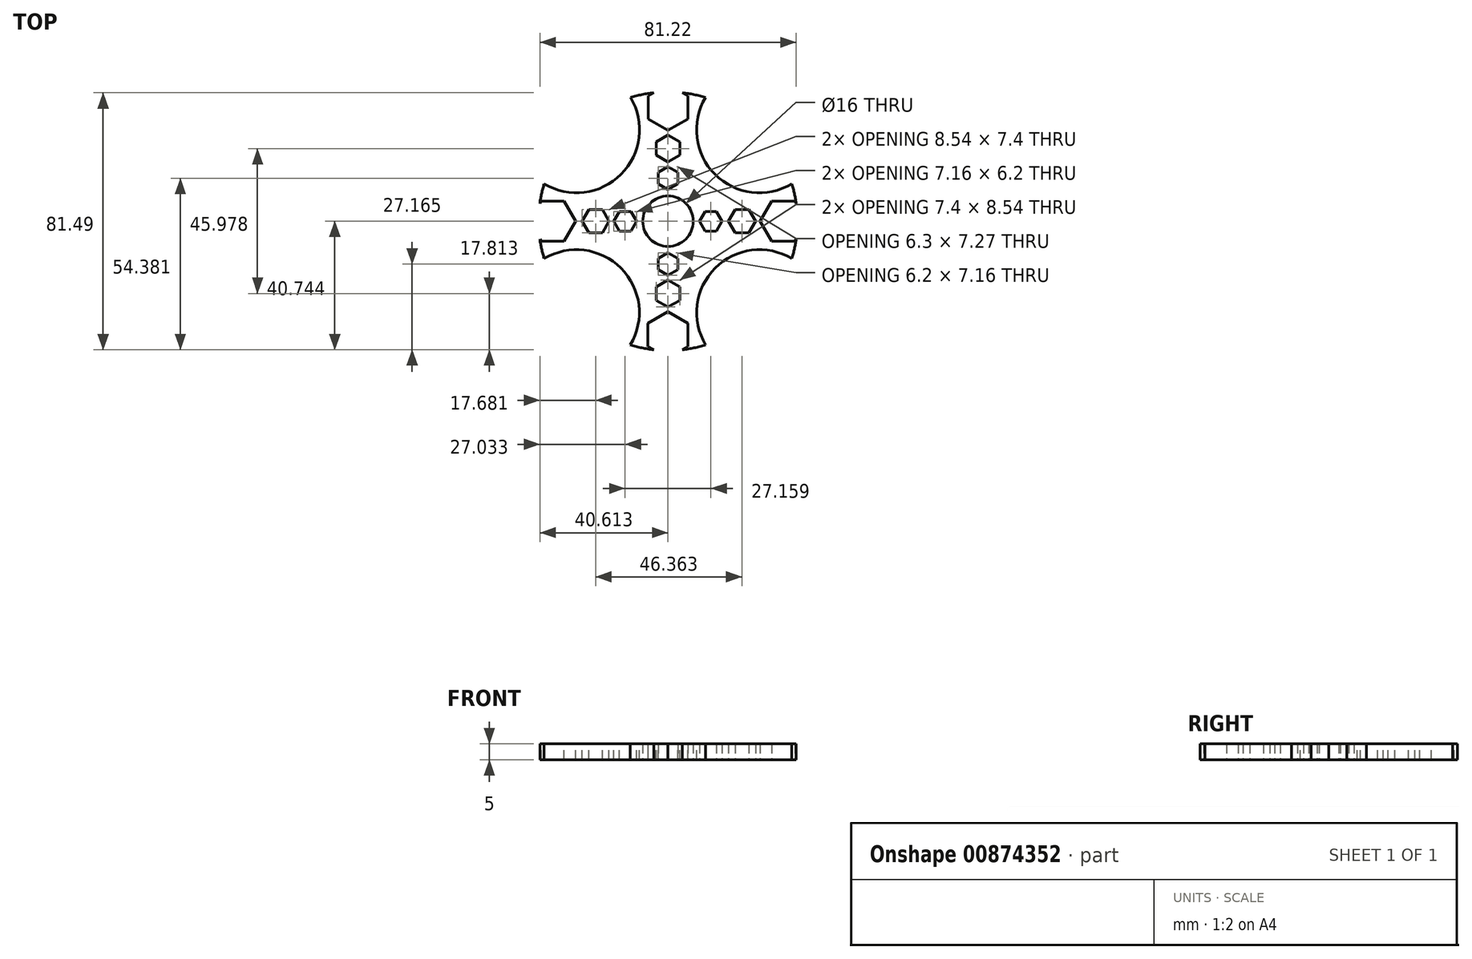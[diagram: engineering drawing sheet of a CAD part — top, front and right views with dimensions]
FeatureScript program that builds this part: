
annotation { "Feature Type Name" : "Feature", "Feature Type Description" : "" }
export const myFeature = defineFeature(function(context is Context, id is Id, definition is map)
    precondition{}
    {
        {
            var Q0;
            Q0=qCreatedBy(makeId("Top.planeOp"),FACE);
            var sketch = newSketch(context, id + "F0", { "sketchPlane" : qUnion([Q0])});
            skCircle(sketch, "E0", {"center": v(-41.45, -163.82) * mm, "radius": 41 * mm});
            skCircle(sketch, "E1", {"center": v(-41.45, -163.82) * mm, "radius": 8 * mm});
            skSolve(sketch);
        }
        {
            var Q0;
            Q0=makeQuery(id+"F0.imprint","IMPRINT",FACE,{"disambiguationData":[TD([[makeQuery(id+"F0.imprint","IMPRINT",EDGE,{"derivedFrom":sQuery(id+"F0.wireOp",EDGE,"E0")}),1.0]])]});
            var sketch = newSketch(context, id + "F1", { "sketchPlane" : qUnion([Q0])});
            skSolve(sketch);
        }
        {
            var Q0;
            Q0 = qSketchRegion(id + "F1", true);
            var Q1;
            Q1=makeQuery(id+"F0.imprint","IMPRINT",FACE,{"disambiguationData":[TD([[makeQuery(id+"F0.imprint","IMPRINT",EDGE,{"derivedFrom":sQuery(id+"F0.wireOp",EDGE,"E0")}),1.0]])]});
            extrude(context, id + "F2", {"entities" : qUnion([Q0, Q1]), "depth" : 5 * mm, "offsetDistance" : 25 * mm});
        }
        {
            var Q0;
            Q0=makeQuery(id+"F1.imprint","IMPRINT",FACE,{"disambiguationData":[TD([[makeQuery(id+"F1.imprint","IMPRINT",EDGE,{"derivedFrom":makeQuery(id+"F0.imprint","IMPRINT",EDGE,{"derivedFrom":sQuery(id+"F0.wireOp",EDGE,"E1")})}),1.0]])]});
            var sketch = newSketch(context, id + "F3", { "sketchPlane" : qUnion([Q0])});
            skSolve(sketch);
        }
        {
            var Q0;
            Q0=makeQuery(id+"F2.opExtrude","CAP_FACE",FACE,{"disambiguationData":[OSD([sQuery(id+"F0.wireOp",EDGE,"E0"),sQuery(id+"F0.wireOp",EDGE,"E1")])],"isStart":false});
            var sketch = newSketch(context, id + "F4", { "sketchPlane" : qUnion([Q0])});
            skCircle(sketch, "E2.cCircle", {"center": v(-41.45, -150.18) * mm, "radius": 3.15 * mm, "construction": true});
            skLineSegment(sketch, "E2.0", {"start": v(-38.3, -148.36) * mm, "end": v(-38.3, -152) * mm});
            skLineSegment(sketch, "E2.1", {"start": v(-38.3, -152) * mm, "end": v(-41.45, -153.82) * mm});
            skLineSegment(sketch, "E2.2", {"start": v(-41.45, -153.82) * mm, "end": v(-44.6, -152) * mm});
            skLineSegment(sketch, "E2.3", {"start": v(-44.6, -152) * mm, "end": v(-44.6, -148.36) * mm});
            skLineSegment(sketch, "E2.4", {"start": v(-44.6, -148.36) * mm, "end": v(-41.45, -146.54) * mm});
            skLineSegment(sketch, "E2.5", {"start": v(-41.45, -146.54) * mm, "end": v(-38.3, -148.36) * mm});
            skPoint(sketch, "E2.0.midPoint", {"position": v(-38.3, -150.18) * mm});
            skCircle(sketch, "E3.0", {"center": v(-41.45, -163.82) * mm, "radius": 8 * mm});
            skLineSegment(sketch, "E4", {"start": v(-41.45, -163.82) * mm, "end": v(-41.45, -137.03) * mm, "construction": true});
            skSolve(sketch);
        }
        {
            var Q0;
            Q0=makeQuery(id+"F4.imprint","IMPRINT",FACE,{"disambiguationData":[TD([[makeQuery(id+"F4.imprint","IMPRINT",EDGE,{"derivedFrom":sQuery(id+"F4.wireOp",EDGE,"E2.0")}),-1.0]])]});
            extrude(context, id + "F5", {"entities" : qUnion([Q0]), "operationType" : NewBodyOperationType.REMOVE, "endBound" : BoundingType.THROUGH_ALL, "oppositeDirection" : true, "depth" : 25 * mm, "offsetDistance" : 25 * mm});
        }
        {
            var Q0;
            Q0=makeQuery(id+"F2.opExtrude","CAP_FACE",FACE,{"disambiguationData":[OSD([sQuery(id+"F0.wireOp",EDGE,"E0"),sQuery(id+"F0.wireOp",EDGE,"E1")])],"isStart":false});
            var sketch = newSketch(context, id + "F6", { "sketchPlane" : qUnion([Q0])});
            skCircle(sketch, "E5.cCircle", {"center": v(-41.45, -140.77) * mm, "radius": 3.7 * mm, "construction": true});
            skLineSegment(sketch, "E5.0", {"start": v(-37.75, -138.63) * mm, "end": v(-37.75, -142.9) * mm});
            skLineSegment(sketch, "E5.1", {"start": v(-37.75, -142.9) * mm, "end": v(-41.45, -145.04) * mm});
            skLineSegment(sketch, "E5.2", {"start": v(-41.45, -145.04) * mm, "end": v(-45.15, -142.9) * mm});
            skLineSegment(sketch, "E5.3", {"start": v(-45.15, -142.9) * mm, "end": v(-45.15, -138.63) * mm});
            skLineSegment(sketch, "E5.4", {"start": v(-45.15, -138.63) * mm, "end": v(-41.45, -136.5) * mm});
            skLineSegment(sketch, "E5.5", {"start": v(-41.45, -136.5) * mm, "end": v(-37.75, -138.63) * mm});
            skPoint(sketch, "E5.0.midPoint", {"position": v(-37.75, -140.77) * mm});
            skSolve(sketch);
        }
        {
            var Q0;
            Q0 = qSketchRegion(id + "F6", true);
            extrude(context, id + "F7", {"entities" : qUnion([Q0]), "operationType" : NewBodyOperationType.REMOVE, "endBound" : BoundingType.THROUGH_ALL, "oppositeDirection" : true, "depth" : 25 * mm, "offsetDistance" : 25 * mm});
        }
        {
            var Q0;
            Q0=makeQuery(id+"F2.opExtrude","CAP_FACE",FACE,{"disambiguationData":[OSD([sQuery(id+"F0.wireOp",EDGE,"E0"),sQuery(id+"F0.wireOp",EDGE,"E1")])],"isStart":false});
            var sketch = newSketch(context, id + "F8", { "sketchPlane" : qUnion([Q0])});
            skCircle(sketch, "E6.cCircle", {"center": v(-41.45, -127.72) * mm, "radius": 6.3 * mm, "construction": true});
            skLineSegment(sketch, "E6.0", {"start": v(-41.45, -135) * mm, "end": v(-47.75, -131.36) * mm});
            skLineSegment(sketch, "E6.1", {"start": v(-47.75, -131.36) * mm, "end": v(-47.75, -124.08) * mm});
            skLineSegment(sketch, "E6.2", {"start": v(-47.75, -124.08) * mm, "end": v(-41.45, -120.45) * mm});
            skLineSegment(sketch, "E6.3", {"start": v(-41.45, -120.45) * mm, "end": v(-35.15, -124.08) * mm});
            skLineSegment(sketch, "E6.4", {"start": v(-35.15, -124.08) * mm, "end": v(-35.15, -131.36) * mm});
            skLineSegment(sketch, "E6.5", {"start": v(-35.15, -131.36) * mm, "end": v(-41.45, -135) * mm});
            skPoint(sketch, "E6.0.midPoint", {"position": v(-44.6, -133.18) * mm});
            skSolve(sketch);
        }
        {
            var Q0;
            Q0 = qSketchRegion(id + "F8", true);
            extrude(context, id + "F9", {"entities" : qUnion([Q0]), "operationType" : NewBodyOperationType.REMOVE, "endBound" : BoundingType.THROUGH_ALL, "oppositeDirection" : true, "depth" : 25 * mm, "offsetDistance" : 25 * mm});
        }
        {
            var Q0;
            Q0=makeQuery(id+"F1.imprint","IMPRINT",FACE,{"disambiguationData":[TD([[makeQuery(id+"F1.imprint","IMPRINT",EDGE,{"derivedFrom":makeQuery(id+"F0.imprint","IMPRINT",EDGE,{"derivedFrom":sQuery(id+"F0.wireOp",EDGE,"E0")})}),1.0]])]});
            var sketch = newSketch(context, id + "F10", { "sketchPlane" : qUnion([Q0])});
            skCircle(sketch, "E7.cCircle", {"center": v(-41.45, -177.4) * mm, "radius": 3.1 * mm, "construction": true});
            skLineSegment(sketch, "E7.0", {"start": v(-41.45, -173.82) * mm, "end": v(-38.35, -175.6) * mm});
            skLineSegment(sketch, "E7.1", {"start": v(-38.35, -175.6) * mm, "end": v(-38.35, -179.19) * mm});
            skLineSegment(sketch, "E7.2", {"start": v(-38.35, -179.19) * mm, "end": v(-41.45, -180.97) * mm});
            skLineSegment(sketch, "E7.3", {"start": v(-41.45, -180.97) * mm, "end": v(-44.55, -179.19) * mm});
            skLineSegment(sketch, "E7.4", {"start": v(-44.55, -179.19) * mm, "end": v(-44.55, -175.6) * mm});
            skLineSegment(sketch, "E7.5", {"start": v(-44.55, -175.6) * mm, "end": v(-41.45, -173.82) * mm});
            skPoint(sketch, "E7.0.midPoint", {"position": v(-39.9, -174.71) * mm});
            skSolve(sketch);
        }
        {
            var Q0;
            Q0=makeQuery(id+"F10.imprint","IMPRINT",FACE,{"disambiguationData":[TD([[makeQuery(id+"F10.imprint","IMPRINT",EDGE,{"derivedFrom":sQuery(id+"F10.wireOp",EDGE,"E7.0")}),-1.0]])]});
            extrude(context, id + "F11", {"entities" : qUnion([Q0]), "operationType" : NewBodyOperationType.REMOVE, "endBound" : BoundingType.THROUGH_ALL, "depth" : 25 * mm, "offsetDistance" : 25 * mm});
        }
        {
            var Q0;
            Q0=makeQuery(id+"F1.imprint","IMPRINT",FACE,{"disambiguationData":[TD([[makeQuery(id+"F1.imprint","IMPRINT",EDGE,{"derivedFrom":makeQuery(id+"F0.imprint","IMPRINT",EDGE,{"derivedFrom":sQuery(id+"F0.wireOp",EDGE,"E0")})}),1.0]])]});
            var sketch = newSketch(context, id + "F12", { "sketchPlane" : qUnion([Q0])});
            skCircle(sketch, "E8.cCircle", {"center": v(-41.45, -186.75) * mm, "radius": 3.7 * mm, "construction": true});
            skLineSegment(sketch, "E8.0", {"start": v(-41.45, -182.47) * mm, "end": v(-37.75, -184.61) * mm});
            skLineSegment(sketch, "E8.1", {"start": v(-37.75, -184.61) * mm, "end": v(-37.75, -188.88) * mm});
            skLineSegment(sketch, "E8.2", {"start": v(-37.75, -188.88) * mm, "end": v(-41.45, -191.02) * mm});
            skLineSegment(sketch, "E8.3", {"start": v(-41.45, -191.02) * mm, "end": v(-45.15, -188.88) * mm});
            skLineSegment(sketch, "E8.4", {"start": v(-45.15, -188.88) * mm, "end": v(-45.15, -184.61) * mm});
            skLineSegment(sketch, "E8.5", {"start": v(-45.15, -184.61) * mm, "end": v(-41.45, -182.47) * mm});
            skPoint(sketch, "E8.0.midPoint", {"position": v(-39.6, -183.54) * mm});
            skSolve(sketch);
        }
        {
            var Q0;
            Q0=makeQuery(id+"F12.imprint","IMPRINT",FACE,{"disambiguationData":[TD([[makeQuery(id+"F12.imprint","IMPRINT",EDGE,{"derivedFrom":sQuery(id+"F12.wireOp",EDGE,"E8.0")}),-1.0]])]});
            extrude(context, id + "F13", {"entities" : qUnion([Q0]), "operationType" : NewBodyOperationType.REMOVE, "endBound" : BoundingType.THROUGH_ALL, "depth" : 25 * mm, "offsetDistance" : 25 * mm});
        }
        {
            var Q0;
            Q0=makeQuery(id+"F1.imprint","IMPRINT",FACE,{"disambiguationData":[TD([[makeQuery(id+"F1.imprint","IMPRINT",EDGE,{"derivedFrom":makeQuery(id+"F0.imprint","IMPRINT",EDGE,{"derivedFrom":sQuery(id+"F0.wireOp",EDGE,"E0")})}),1.0]])]});
            var sketch = newSketch(context, id + "F14", { "sketchPlane" : qUnion([Q0])});
            skCircle(sketch, "E9.cCircle", {"center": v(-41.45, -199.85) * mm, "radius": 6.35 * mm, "construction": true});
            skLineSegment(sketch, "E9.0", {"start": v(-41.45, -192.52) * mm, "end": v(-35.1, -196.19) * mm});
            skLineSegment(sketch, "E9.1", {"start": v(-35.1, -196.19) * mm, "end": v(-35.1, -203.52) * mm});
            skLineSegment(sketch, "E9.2", {"start": v(-35.1, -203.52) * mm, "end": v(-41.45, -207.18) * mm});
            skLineSegment(sketch, "E9.3", {"start": v(-41.45, -207.18) * mm, "end": v(-47.8, -203.52) * mm});
            skLineSegment(sketch, "E9.4", {"start": v(-47.8, -203.52) * mm, "end": v(-47.8, -196.19) * mm});
            skLineSegment(sketch, "E9.5", {"start": v(-47.8, -196.19) * mm, "end": v(-41.45, -192.52) * mm});
            skPoint(sketch, "E9.0.midPoint", {"position": v(-38.27, -194.35) * mm});
            skSolve(sketch);
        }
        {
            var Q0;
            Q0=makeQuery(id+"F14.imprint","IMPRINT",FACE,{"disambiguationData":[TD([[makeQuery(id+"F14.imprint","IMPRINT",EDGE,{"derivedFrom":sQuery(id+"F14.wireOp",EDGE,"E9.0")}),-1.0]])]});
            extrude(context, id + "F15", {"entities" : qUnion([Q0]), "operationType" : NewBodyOperationType.REMOVE, "depth" : 25 * mm, "offsetDistance" : 25 * mm});
        }
        {
            var Q0;
            Q0=makeQuery(id+"F1.imprint","IMPRINT",FACE,{"disambiguationData":[TD([[makeQuery(id+"F1.imprint","IMPRINT",EDGE,{"derivedFrom":makeQuery(id+"F0.imprint","IMPRINT",EDGE,{"derivedFrom":sQuery(id+"F0.wireOp",EDGE,"E0")})}),1.0]])]});
            var sketch = newSketch(context, id + "F16", { "sketchPlane" : qUnion([Q0])});
            skCircle(sketch, "E10.cCircle", {"center": v(-27.87, -163.82) * mm, "radius": 3.1 * mm, "construction": true});
            skLineSegment(sketch, "E10.0", {"start": v(-26.08, -160.72) * mm, "end": v(-24.29, -163.82) * mm});
            skLineSegment(sketch, "E10.1", {"start": v(-24.29, -163.82) * mm, "end": v(-26.08, -166.92) * mm});
            skLineSegment(sketch, "E10.2", {"start": v(-26.08, -166.92) * mm, "end": v(-29.66, -166.92) * mm});
            skLineSegment(sketch, "E10.3", {"start": v(-29.66, -166.92) * mm, "end": v(-31.45, -163.82) * mm});
            skLineSegment(sketch, "E10.4", {"start": v(-31.45, -163.82) * mm, "end": v(-29.66, -160.72) * mm});
            skLineSegment(sketch, "E10.5", {"start": v(-29.66, -160.72) * mm, "end": v(-26.08, -160.72) * mm});
            skPoint(sketch, "E10.0.midPoint", {"position": v(-25.18, -162.27) * mm});
            skCircle(sketch, "E11.0", {"center": v(-41.45, -163.82) * mm, "radius": 8 * mm});
            skLineSegment(sketch, "E12", {"start": v(-41.45, -163.82) * mm, "end": v(9.91, -163.82) * mm});
            skSolve(sketch);
        }
        {
            var Q0;
            Q0 = qSketchRegion(id + "F16", true);
            extrude(context, id + "F17", {"entities" : qUnion([Q0]), "operationType" : NewBodyOperationType.REMOVE, "endBound" : BoundingType.THROUGH_ALL, "depth" : 25 * mm, "offsetDistance" : 25 * mm});
        }
        {
            var Q0;
            Q0=makeQuery(id+"F1.imprint","IMPRINT",FACE,{"disambiguationData":[TD([[makeQuery(id+"F1.imprint","IMPRINT",EDGE,{"derivedFrom":makeQuery(id+"F0.imprint","IMPRINT",EDGE,{"derivedFrom":sQuery(id+"F0.wireOp",EDGE,"E0")})}),1.0]])]});
            var sketch = newSketch(context, id + "F18", { "sketchPlane" : qUnion([Q0])});
            skCircle(sketch, "E13.cCircle", {"center": v(-18.02, -163.82) * mm, "radius": 3.7 * mm, "construction": true});
            skLineSegment(sketch, "E13.0", {"start": v(-20.15, -160.12) * mm, "end": v(-15.88, -160.12) * mm});
            skLineSegment(sketch, "E13.1", {"start": v(-15.88, -160.12) * mm, "end": v(-13.74, -163.82) * mm});
            skLineSegment(sketch, "E13.2", {"start": v(-13.74, -163.82) * mm, "end": v(-15.88, -167.52) * mm});
            skLineSegment(sketch, "E13.3", {"start": v(-15.88, -167.52) * mm, "end": v(-20.15, -167.52) * mm});
            skLineSegment(sketch, "E13.4", {"start": v(-20.15, -167.52) * mm, "end": v(-22.29, -163.82) * mm});
            skLineSegment(sketch, "E13.5", {"start": v(-22.29, -163.82) * mm, "end": v(-20.15, -160.12) * mm});
            skPoint(sketch, "E13.0.midPoint", {"position": v(-18.02, -160.12) * mm});
            skCircle(sketch, "E14.0.0", {"center": v(-41.45, -163.82) * mm, "radius": 8 * mm});
            skLineSegment(sketch, "E15", {"start": v(-41.45, -163.82) * mm, "end": v(10.87, -163.82) * mm, "construction": true});
            skSolve(sketch);
        }
        {
            var Q0;
            Q0=makeQuery(id+"F18.imprint","IMPRINT",FACE,{"disambiguationData":[TD([[makeQuery(id+"F18.imprint","IMPRINT",EDGE,{"derivedFrom":sQuery(id+"F18.wireOp",EDGE,"E13.0")}),-1.0]])]});
            extrude(context, id + "F19", {"entities" : qUnion([Q0]), "operationType" : NewBodyOperationType.REMOVE, "endBound" : BoundingType.THROUGH_ALL, "depth" : 25 * mm, "offsetDistance" : 25 * mm});
        }
        {
            var Q0;
            Q0=makeQuery(id+"F1.imprint","IMPRINT",FACE,{"disambiguationData":[TD([[makeQuery(id+"F1.imprint","IMPRINT",EDGE,{"derivedFrom":makeQuery(id+"F0.imprint","IMPRINT",EDGE,{"derivedFrom":sQuery(id+"F0.wireOp",EDGE,"E0")})}),1.0]])]});
            var sketch = newSketch(context, id + "F20", { "sketchPlane" : qUnion([Q0])});
            skCircle(sketch, "E16.cCircle", {"center": v(-4.91, -163.82) * mm, "radius": 6.35 * mm, "construction": true});
            skLineSegment(sketch, "E16.0", {"start": v(-1.24, -157.47) * mm, "end": v(2.42, -163.82) * mm});
            skLineSegment(sketch, "E16.1", {"start": v(2.42, -163.82) * mm, "end": v(-1.24, -170.17) * mm});
            skLineSegment(sketch, "E16.2", {"start": v(-1.24, -170.17) * mm, "end": v(-8.58, -170.17) * mm});
            skLineSegment(sketch, "E16.3", {"start": v(-8.58, -170.17) * mm, "end": v(-12.24, -163.82) * mm});
            skLineSegment(sketch, "E16.4", {"start": v(-12.24, -163.82) * mm, "end": v(-8.58, -157.47) * mm});
            skLineSegment(sketch, "E16.5", {"start": v(-8.58, -157.47) * mm, "end": v(-1.24, -157.47) * mm});
            skPoint(sketch, "E16.0.midPoint", {"position": v(0.59, -160.64) * mm});
            skSolve(sketch);
        }
        {
            var Q0;
            {var subQ0=sQuery(id+"F20.wireOp",EDGE,"E16.2");Q0=makeQuery(id+"F20.imprint","IMPRINT",FACE,{"disambiguationData":[TD([[makeQuery(id+"F20.imprint","IMPRINT",EDGE,{"derivedFrom":subQ0}),-1.0]])]});}
            extrude(context, id + "F21", {"entities" : qUnion([Q0]), "operationType" : NewBodyOperationType.REMOVE, "endBound" : BoundingType.THROUGH_ALL, "depth" : 25 * mm, "offsetDistance" : 25 * mm});
        }
        {
            var Q0;
            Q0=makeQuery(id+"F2.opExtrude","CAP_FACE",FACE,{"disambiguationData":[OSD([sQuery(id+"F0.wireOp",EDGE,"E0"),sQuery(id+"F0.wireOp",EDGE,"E1")])],"isStart":false});
            var sketch = newSketch(context, id + "F22", { "sketchPlane" : qUnion([Q0])});
            skCircle(sketch, "E17.cCircle", {"center": v(-55.03, -163.82) * mm, "radius": 3.1 * mm, "construction": true});
            skLineSegment(sketch, "E17.0", {"start": v(-56.82, -160.72) * mm, "end": v(-53.24, -160.72) * mm});
            skLineSegment(sketch, "E17.1", {"start": v(-53.24, -160.72) * mm, "end": v(-51.45, -163.82) * mm});
            skLineSegment(sketch, "E17.2", {"start": v(-51.45, -163.82) * mm, "end": v(-53.24, -166.92) * mm});
            skLineSegment(sketch, "E17.3", {"start": v(-53.24, -166.92) * mm, "end": v(-56.82, -166.92) * mm});
            skLineSegment(sketch, "E17.4", {"start": v(-56.82, -166.92) * mm, "end": v(-58.6, -163.82) * mm});
            skLineSegment(sketch, "E17.5", {"start": v(-58.6, -163.82) * mm, "end": v(-56.82, -160.72) * mm});
            skPoint(sketch, "E17.0.midPoint", {"position": v(-55.03, -160.72) * mm});
            skCircle(sketch, "E18.0.0", {"center": v(-41.45, -163.82) * mm, "radius": 8 * mm});
            skLineSegment(sketch, "E19", {"start": v(-41.45, -163.82) * mm, "end": v(-87.03, -163.82) * mm, "construction": true});
            skSolve(sketch);
        }
        {
            var Q0;
            Q0 = qSketchRegion(id + "F22", true);
            extrude(context, id + "F23", {"entities" : qUnion([Q0]), "operationType" : NewBodyOperationType.REMOVE, "endBound" : BoundingType.THROUGH_ALL, "oppositeDirection" : true, "depth" : 25 * mm, "offsetDistance" : 25 * mm});
        }
        {
            var Q0;
            Q0=makeQuery(id+"F2.opExtrude","CAP_FACE",FACE,{"disambiguationData":[OSD([sQuery(id+"F0.wireOp",EDGE,"E0"),sQuery(id+"F0.wireOp",EDGE,"E1")])],"isStart":false});
            var sketch = newSketch(context, id + "F24", { "sketchPlane" : qUnion([Q0])});
            skCircle(sketch, "E20.cCircle", {"center": v(-64.38, -163.82) * mm, "radius": 3.7 * mm, "construction": true});
            skLineSegment(sketch, "E20.0", {"start": v(-62.24, -160.12) * mm, "end": v(-60.1, -163.82) * mm});
            skLineSegment(sketch, "E20.1", {"start": v(-60.1, -163.82) * mm, "end": v(-62.24, -167.52) * mm});
            skLineSegment(sketch, "E20.2", {"start": v(-62.24, -167.52) * mm, "end": v(-66.52, -167.52) * mm});
            skLineSegment(sketch, "E20.3", {"start": v(-66.52, -167.52) * mm, "end": v(-68.65, -163.82) * mm});
            skLineSegment(sketch, "E20.4", {"start": v(-68.65, -163.82) * mm, "end": v(-66.52, -160.12) * mm});
            skLineSegment(sketch, "E20.5", {"start": v(-66.52, -160.12) * mm, "end": v(-62.24, -160.12) * mm});
            skPoint(sketch, "E20.0.midPoint", {"position": v(-61.17, -161.97) * mm});
            skCircle(sketch, "E21.0.0", {"center": v(-41.45, -163.82) * mm, "radius": 8 * mm});
            skLineSegment(sketch, "E22", {"start": v(-41.45, -163.82) * mm, "end": v(-86.16, -163.82) * mm, "construction": true});
            skSolve(sketch);
        }
        {
            var Q0;
            Q0 = qSketchRegion(id + "F24", true);
            extrude(context, id + "F25", {"entities" : qUnion([Q0]), "operationType" : NewBodyOperationType.REMOVE, "endBound" : BoundingType.THROUGH_ALL, "oppositeDirection" : true, "depth" : 25 * mm, "offsetDistance" : 25 * mm});
        }
        {
            var Q0;
            Q0=makeQuery(id+"F2.opExtrude","CAP_FACE",FACE,{"disambiguationData":[OSD([sQuery(id+"F0.wireOp",EDGE,"E0"),sQuery(id+"F0.wireOp",EDGE,"E1")])],"isStart":false});
            var sketch = newSketch(context, id + "F26", { "sketchPlane" : qUnion([Q0])});
            skCircle(sketch, "E23.cCircle", {"center": v(-77.98, -163.82) * mm, "radius": 6.35 * mm, "construction": true});
            skLineSegment(sketch, "E23.0", {"start": v(-81.65, -170.17) * mm, "end": v(-85.32, -163.82) * mm});
            skLineSegment(sketch, "E23.1", {"start": v(-85.32, -163.82) * mm, "end": v(-81.65, -157.47) * mm});
            skLineSegment(sketch, "E23.2", {"start": v(-81.65, -157.47) * mm, "end": v(-74.32, -157.47) * mm});
            skLineSegment(sketch, "E23.3", {"start": v(-74.32, -157.47) * mm, "end": v(-70.65, -163.82) * mm});
            skLineSegment(sketch, "E23.4", {"start": v(-70.65, -163.82) * mm, "end": v(-74.32, -170.17) * mm});
            skLineSegment(sketch, "E23.5", {"start": v(-74.32, -170.17) * mm, "end": v(-81.65, -170.17) * mm});
            skPoint(sketch, "E23.0.midPoint", {"position": v(-83.48, -167) * mm});
            skCircle(sketch, "E24.0.0", {"center": v(-41.45, -163.82) * mm, "radius": 8 * mm});
            skLineSegment(sketch, "E25", {"start": v(-41.45, -163.82) * mm, "end": v(-94.13, -163.82) * mm, "construction": true});
            skSolve(sketch);
        }
        {
            var Q0;
            Q0 = qSketchRegion(id + "F26", true);
            extrude(context, id + "F27", {"entities" : qUnion([Q0]), "operationType" : NewBodyOperationType.REMOVE, "endBound" : BoundingType.THROUGH_ALL, "oppositeDirection" : true, "depth" : 25 * mm, "offsetDistance" : 25 * mm});
        }
        {
            var Q0;
            Q0=makeQuery(id+"F2.opExtrude","CAP_FACE",FACE,{"disambiguationData":[OSD([sQuery(id+"F0.wireOp",EDGE,"E0"),sQuery(id+"F0.wireOp",EDGE,"E1")])],"isStart":false});
            var sketch = newSketch(context, id + "F28", { "sketchPlane" : qUnion([Q0])});
            skCircle(sketch, "E26", {"center": v(-70.47, -192.77) * mm, "radius": 19.93 * mm});
            skSolve(sketch);
        }
        {
            var Q0;
            Q0 = qSketchRegion(id + "F28", true);
            extrude(context, id + "F29", {"entities" : qUnion([Q0]), "operationType" : NewBodyOperationType.REMOVE, "endBound" : BoundingType.THROUGH_ALL, "oppositeDirection" : true, "depth" : 25 * mm, "offsetDistance" : 25 * mm});
        }
        {
            var Q0;
            Q0=makeQuery(id+"F2.opExtrude","CAP_FACE",FACE,{"disambiguationData":[OSD([sQuery(id+"F0.wireOp",EDGE,"E0"),sQuery(id+"F0.wireOp",EDGE,"E1")])],"isStart":false});
            var sketch = newSketch(context, id + "F30", { "sketchPlane" : qUnion([Q0])});
            skCircle(sketch, "E27", {"center": v(-70.45, -134.83) * mm, "radius": 19.96 * mm});
            skSolve(sketch);
        }
        {
            var Q0;
            Q0 = qSketchRegion(id + "F30", true);
            extrude(context, id + "F31", {"entities" : qUnion([Q0]), "operationType" : NewBodyOperationType.REMOVE, "endBound" : BoundingType.THROUGH_ALL, "oppositeDirection" : true, "depth" : 25 * mm, "offsetDistance" : 25 * mm});
        }
        {
            var Q0;
            Q0=makeQuery(id+"F2.opExtrude","CAP_FACE",FACE,{"disambiguationData":[OSD([sQuery(id+"F0.wireOp",EDGE,"E0"),sQuery(id+"F0.wireOp",EDGE,"E1")])],"isStart":false});
            var sketch = newSketch(context, id + "F32", { "sketchPlane" : qUnion([Q0])});
            skCircle(sketch, "E28", {"center": v(-12.45, -134.83) * mm, "radius": 19.96 * mm});
            skSolve(sketch);
        }
        {
            var Q0;
            Q0 = qSketchRegion(id + "F32", true);
            extrude(context, id + "F33", {"entities" : qUnion([Q0]), "operationType" : NewBodyOperationType.REMOVE, "endBound" : BoundingType.THROUGH_ALL, "oppositeDirection" : true, "depth" : 25 * mm, "offsetDistance" : 25 * mm});
        }
        {
            var Q0;
            Q0=makeQuery(id+"F2.opExtrude","CAP_FACE",FACE,{"disambiguationData":[OSD([sQuery(id+"F0.wireOp",EDGE,"E0"),sQuery(id+"F0.wireOp",EDGE,"E1")])],"isStart":false});
            var sketch = newSketch(context, id + "F34", { "sketchPlane" : qUnion([Q0])});
            skCircle(sketch, "E29", {"center": v(-12.42, -192.77) * mm, "radius": 19.93 * mm});
            skSolve(sketch);
        }
        {
            var Q0;
            Q0 = qSketchRegion(id + "F34", true);
            extrude(context, id + "F35", {"entities" : qUnion([Q0]), "operationType" : NewBodyOperationType.REMOVE, "endBound" : BoundingType.THROUGH_ALL, "oppositeDirection" : true, "depth" : 25 * mm, "offsetDistance" : 25 * mm});
        }
    });
